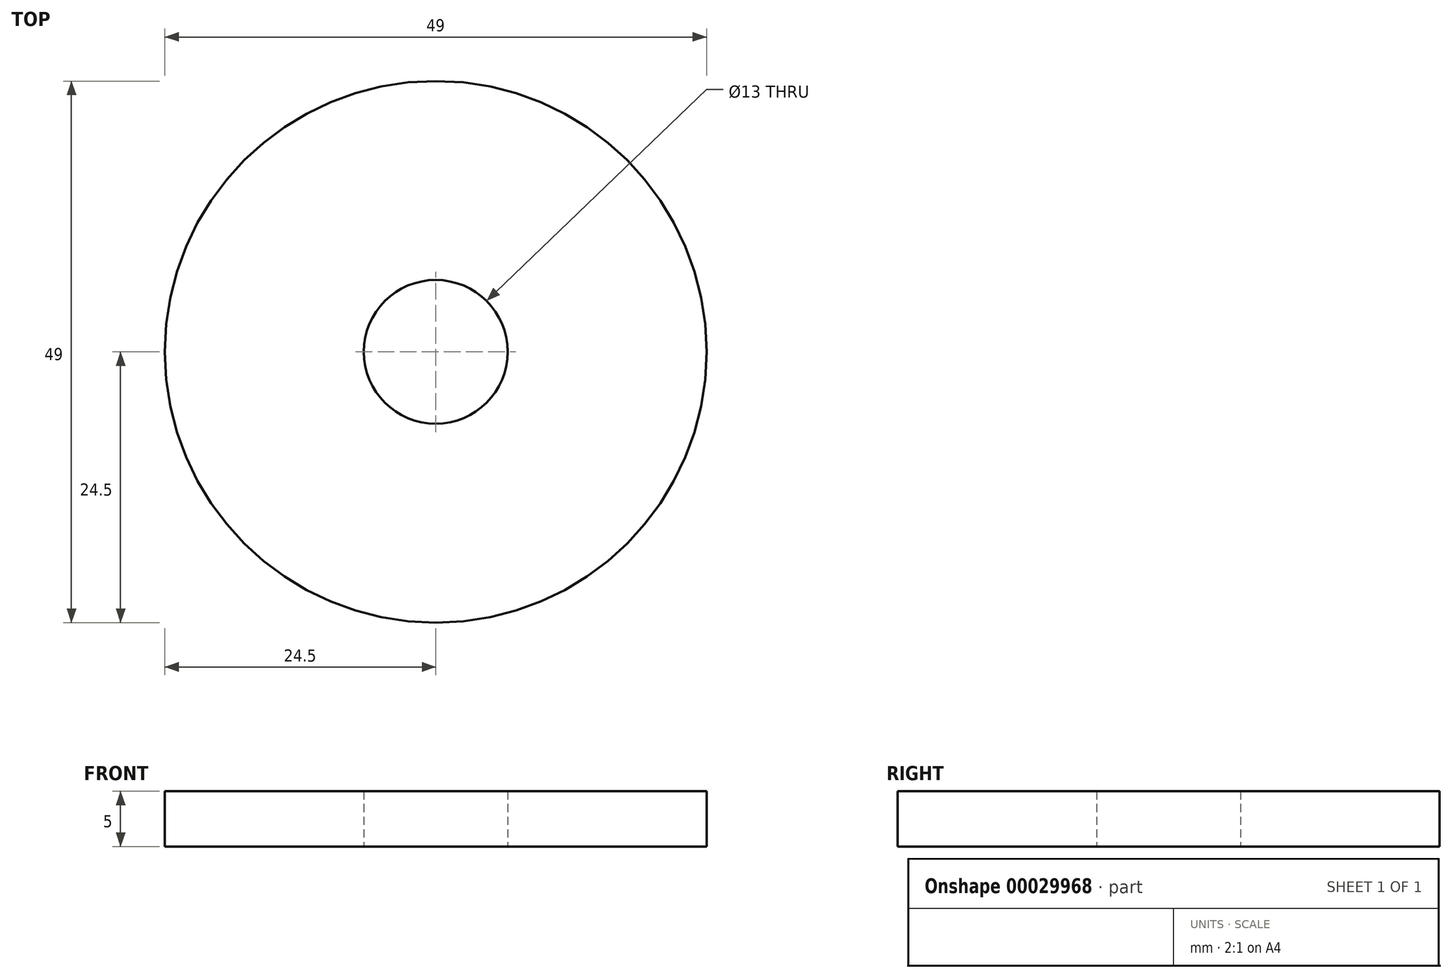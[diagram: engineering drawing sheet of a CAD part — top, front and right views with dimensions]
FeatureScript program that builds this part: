
annotation { "Feature Type Name" : "Feature", "Feature Type Description" : "" }
export const myFeature = defineFeature(function(context is Context, id is Id, definition is map)
    precondition{}
    {
        {
            var Q0;
            Q0=qCreatedBy(makeId("Top.planeOp"),FACE);
            var sketch = newSketch(context, id + "F0", { "sketchPlane" : qUnion([Q0])});
            skCircle(sketch, "E0", {"center": v(0, 0) * mm, "radius": 24.5 * mm});
            skCircle(sketch, "E1", {"center": v(0, 0) * mm, "radius": 6.5 * mm});
            skSolve(sketch);
        }
        {
            var Q0;
            Q0 = qSketchRegion(id + "F0", true);
            extrude(context, id + "F1", {"entities" : qUnion([Q0]), "depth" : 5 * mm});
        }
    });
